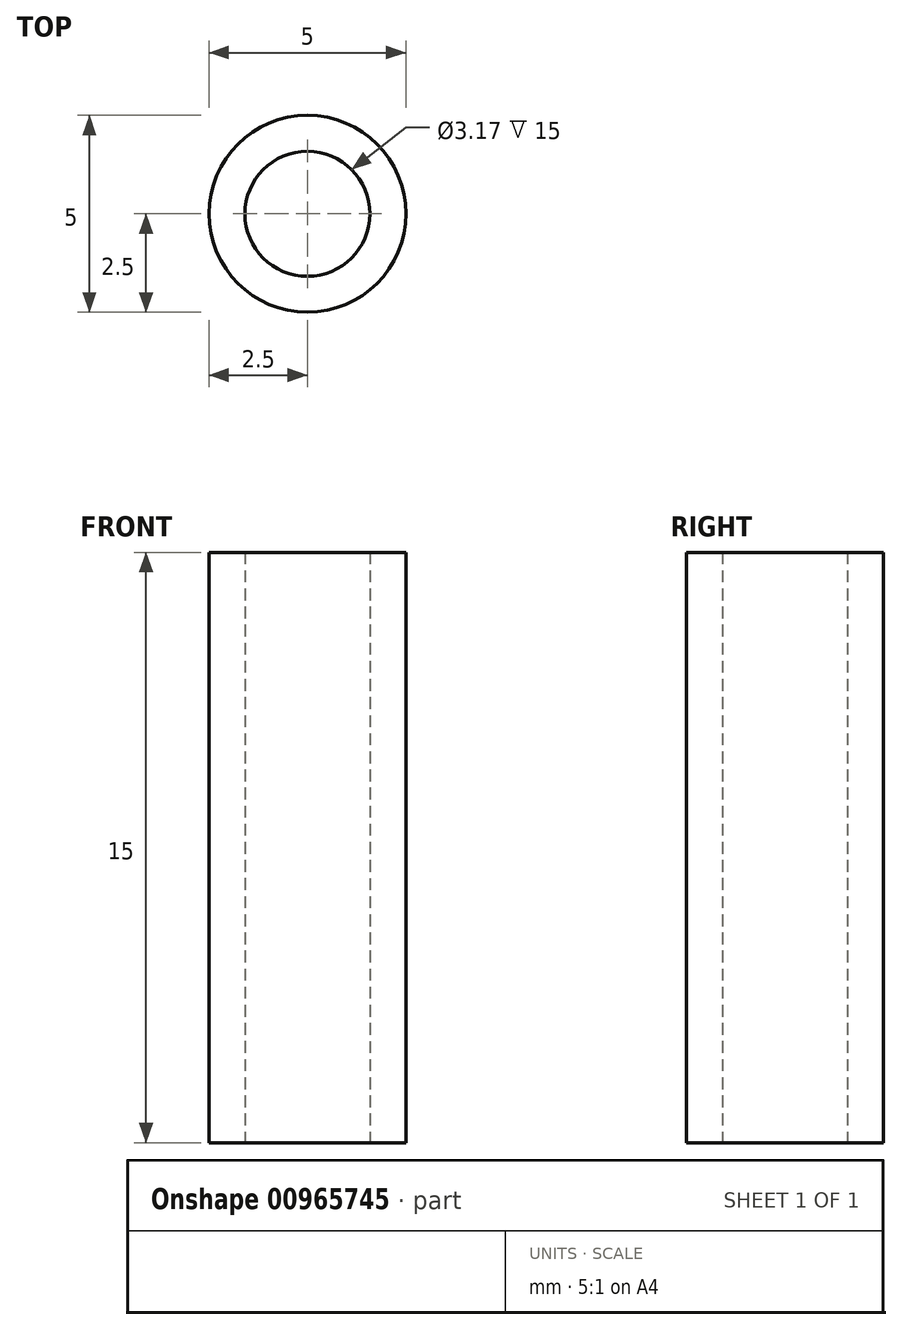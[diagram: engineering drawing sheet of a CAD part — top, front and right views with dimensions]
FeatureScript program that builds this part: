
annotation { "Feature Type Name" : "Feature", "Feature Type Description" : "" }
export const myFeature = defineFeature(function(context is Context, id is Id, definition is map)
    precondition{}
    {
        {
            var Q0;
            Q0=qCreatedBy(makeId("Top.planeOp"),FACE);
            var sketch = newSketch(context, id + "F0", { "sketchPlane" : qUnion([Q0])});
            skCircle(sketch, "E0", {"center": v(0, 0) * mm, "radius": 2.5 * mm});
            skCircle(sketch, "E1", {"center": v(0, 0) * mm, "radius": 1.59 * mm});
            skSolve(sketch);
        }
        {
            var Q0;
            Q0 = qSketchRegion(id + "F0", true);
            extrude(context, id + "F1", {"entities" : qUnion([Q0]), "depth" : 15 * mm, "offsetDistance" : 25 * mm});
        }
    });
